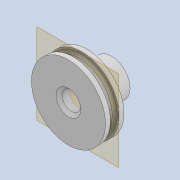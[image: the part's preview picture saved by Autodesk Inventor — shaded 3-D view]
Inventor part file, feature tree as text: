
AUTODESK INVENTOR PART (.ipt)
format: ipt  version: 2020 (Build 240168000, 168)  size: 169,984 bytes
history: native  units: mm
features: extrude x4, sketch x4, other x3, thicken_offset x2, fillet x2, plane x1, chamfer x1, reference x1
ambient origin geometry x8: Origin, YZ Plane, XZ Plane, XY Plane, X Axis, Y Axis, Z Axis, Center Point
bodies: Solid1 (feature_tree)
feature tree (18):
  extrude  "Extrusion1"  Depth=6.0mm
  extrude  "Extrusion2"  Depth=2.0mm
  extrude  "Extrusion3"  Depth=3.0mm
  thicken_offset  "Thicken1"
  plane  "Work Plane1"
  extrude  "Extrusion4"  Depth=2.0mm TaperAngle=0.0deg
  fillet  "Fillet1"  Radius=2.0mm
  fillet  "Fillet2"  Radius=2.0mm
  thicken_offset  "Thicken2"
  chamfer  "Chamfer2"  [1 undecoded]
  sketch  "Sketch1"  dims[d0=3.0mm d1=6.0mm]
  sketch  "Sketch2"  dims[d2=2.0mm d3=0.0mm d4=12.0mm]
  sketch  "Sketch3"  dims[d5=3.0mm d6=0.0mm d7=3.0mm]
  reference  "Reference1"
  sketch  "Sketch4"  dims[d8=6.0mm d9=2.0mm d10=0.0mm d11=2.0mm d12=2.0mm d13=-1.5mm d14=0.7mm d15=1.4mm d16=0.0mm d17=0.4mm d21=1.0mm d22=2.0mm d23=2.0mm d24=0.5mm d25=2.0mm d26=45.0deg]
  parser-record x1  (decoder bookkeeping rows leaked as tree rows — omitted from the tree; the rows remain in map.json)
  other  "tip_3_n_ass.iam"
  other  "pin3_40:2"
note: 1 required parameter value undecoded (feature->parameter linkage not recoverable at this tier; creation-order binding heuristic only, values carry confidence <= 0.55)
note: 1 file-system path scrubbed to <path> (originals preserved in map.json)
